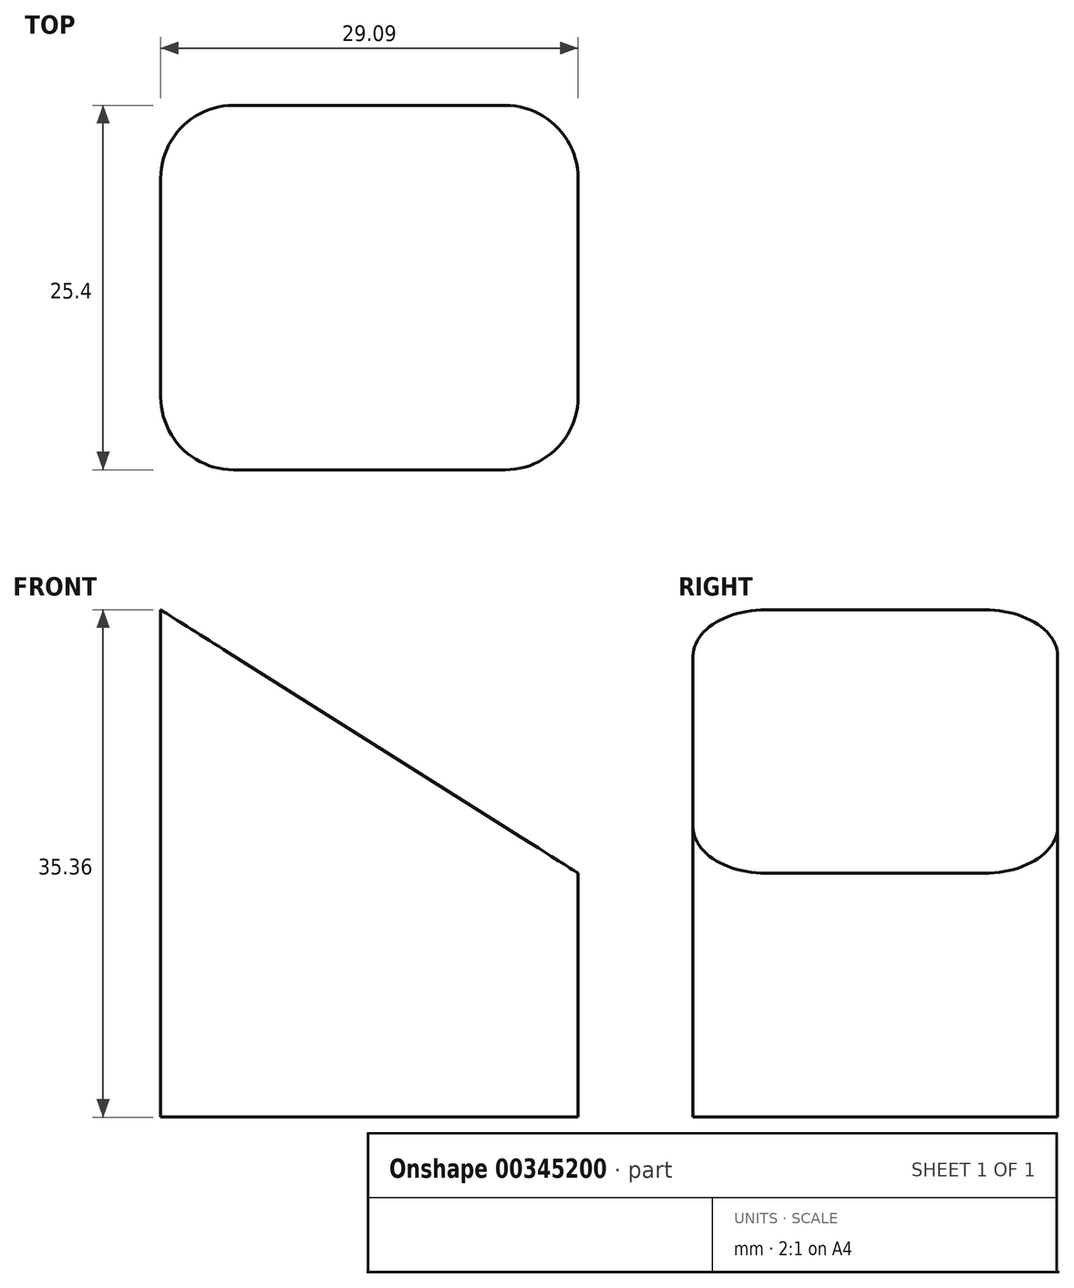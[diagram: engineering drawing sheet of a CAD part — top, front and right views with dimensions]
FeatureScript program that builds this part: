
annotation { "Feature Type Name" : "Feature", "Feature Type Description" : "" }
export const myFeature = defineFeature(function(context is Context, id is Id, definition is map)
    precondition{}
    {
        {
            var Q0;
            Q0=qCreatedBy(makeId("Front.planeOp"),FACE);
            var sketch = newSketch(context, id + "F0", { "sketchPlane" : qUnion([Q0])});
            skLineSegment(sketch, "E0", {"start": v(-25.1, 17.19) * mm, "end": v(-25.1, -18.17) * mm});
            skLineSegment(sketch, "E1", {"start": v(-25.1, -18.17) * mm, "end": v(3.99, -18.17) * mm});
            skLineSegment(sketch, "E2", {"start": v(3.99, -18.17) * mm, "end": v(3.99, -1.17) * mm});
            skLineSegment(sketch, "E3", {"start": v(3.99, -1.17) * mm, "end": v(-25.1, 17.19) * mm});
            skSolve(sketch);
        }
        {
            var Q0;
            Q0 = qSketchRegion(id + "F0", true);
            extrude(context, id + "F1", {"entities" : qUnion([Q0]), "depth" : 25.4 * mm});
        }
        {
            var Q0;
            Q0=makeQuery(id+"F1.opExtrude","CAP_EDGE",EDGE,{"disambiguationData":[OSD([sQuery(id+"F0.wireOp",EDGE,"E2")])],"isStart":false});
            var Q1;
            Q1=makeQuery(id+"F1.opExtrude","CAP_EDGE",EDGE,{"disambiguationData":[OSD([sQuery(id+"F0.wireOp",EDGE,"E0")])],"isStart":false});
            var Q2;
            Q2=makeQuery(id+"F1.opExtrude","CAP_EDGE",EDGE,{"disambiguationData":[OSD([sQuery(id+"F0.wireOp",EDGE,"E2")])],"isStart":true});
            var Q3;
            Q3=makeQuery(id+"F1.opExtrude","CAP_EDGE",EDGE,{"disambiguationData":[OSD([sQuery(id+"F0.wireOp",EDGE,"E0")])],"isStart":true});
            fillet(context, id + "F2", {"entities" : qUnion([Q0, Q1, Q2, Q3]), "radius" : 5.08 * mm, "tangentPropagation" : true, "allowEdgeOverflow" : false});
        }
    });
